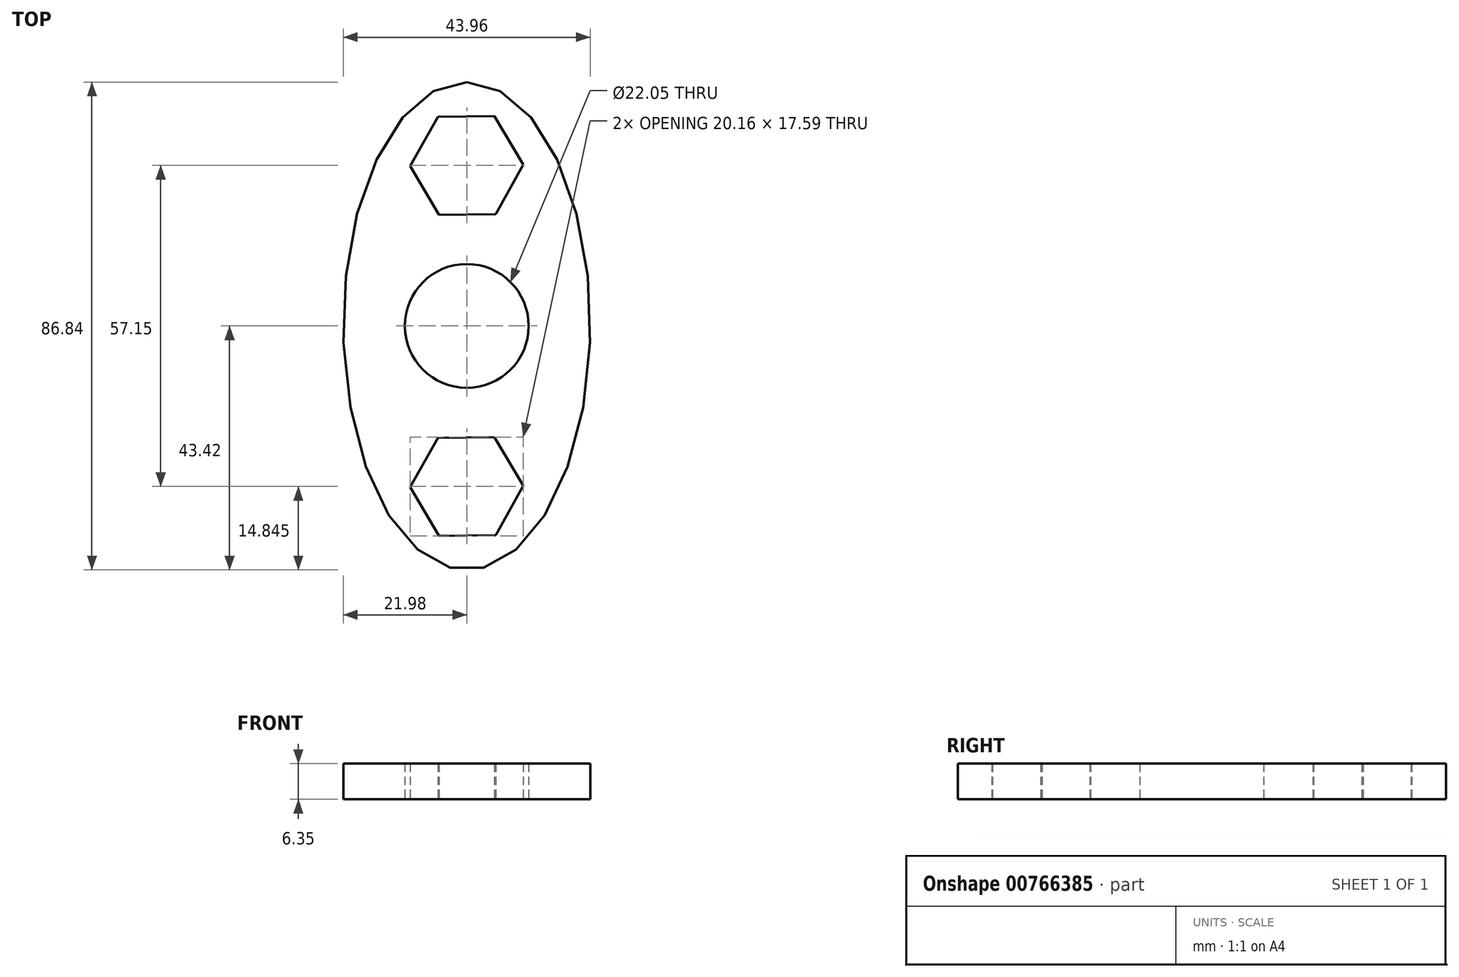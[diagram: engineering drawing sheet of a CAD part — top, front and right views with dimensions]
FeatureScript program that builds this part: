
annotation { "Feature Type Name" : "Feature", "Feature Type Description" : "" }
export const myFeature = defineFeature(function(context is Context, id is Id, definition is map)
    precondition{}
    {
        {
            var Q0;
            Q0=qCreatedBy(makeId("Top.planeOp"),FACE);
            var sketch = newSketch(context, id + "F0", { "sketchPlane" : qUnion([Q0])});
            skCircle(sketch, "E0", {"center": v(0, 0) * mm, "radius": 11.02 * mm});
            skCircle(sketch, "E1", {"center": v(0, 0) * mm, "radius": 14.29 * mm});
            skCircle(sketch, "E2.cCircle", {"center": v(0, 28.58) * mm, "radius": 8.73 * mm, "construction": true});
            skLineSegment(sketch, "E2.0", {"start": v(10.08, 28.7) * mm, "end": v(5.16, 19.91) * mm});
            skLineSegment(sketch, "E2.1", {"start": v(5.16, 19.91) * mm, "end": v(-4.93, 19.78) * mm});
            skLineSegment(sketch, "E2.2", {"start": v(-4.93, 19.78) * mm, "end": v(-10.08, 28.44) * mm});
            skLineSegment(sketch, "E2.3", {"start": v(-10.08, 28.44) * mm, "end": v(-5.16, 37.24) * mm});
            skLineSegment(sketch, "E2.4", {"start": v(-5.16, 37.24) * mm, "end": v(4.93, 37.37) * mm});
            skLineSegment(sketch, "E2.5", {"start": v(4.93, 37.37) * mm, "end": v(10.08, 28.7) * mm});
            skPoint(sketch, "E2.0.midPoint", {"position": v(7.62, 24.3) * mm});
            skCircle(sketch, "E3.cCircle", {"center": v(0, 28.58) * mm, "radius": 11.11 * mm, "construction": true});
            skLineSegment(sketch, "E3.0", {"start": v(6.21, 39.8) * mm, "end": v(12.83, 28.81) * mm});
            skLineSegment(sketch, "E3.1", {"start": v(12.83, 28.81) * mm, "end": v(6.62, 17.58) * mm});
            skLineSegment(sketch, "E3.2", {"start": v(6.62, 17.58) * mm, "end": v(-6.21, 17.35) * mm});
            skLineSegment(sketch, "E3.3", {"start": v(-6.21, 17.35) * mm, "end": v(-12.83, 28.34) * mm});
            skLineSegment(sketch, "E3.4", {"start": v(-12.83, 28.34) * mm, "end": v(-6.62, 39.57) * mm});
            skLineSegment(sketch, "E3.5", {"start": v(-6.62, 39.57) * mm, "end": v(6.21, 39.8) * mm});
            skPoint(sketch, "E3.0.midPoint", {"position": v(9.52, 34.3) * mm});
            skPoint(sketch, "E4.1.0", {"position": v(-9.52, -34.3) * mm});
            skCircle(sketch, "E4.1.1", {"center": v(0, -28.58) * mm, "radius": 8.73 * mm, "construction": true});
            skLineSegment(sketch, "E4.1.2", {"start": v(12.83, -28.34) * mm, "end": v(6.62, -39.57) * mm});
            skLineSegment(sketch, "E4.1.3", {"start": v(6.62, -39.57) * mm, "end": v(-6.21, -39.8) * mm});
            skCircle(sketch, "E4.1.4", {"center": v(0, -28.58) * mm, "radius": 11.11 * mm, "construction": true});
            skPoint(sketch, "E4.1.5", {"position": v(-7.62, -24.3) * mm});
            skLineSegment(sketch, "E4.1.6", {"start": v(5.16, -37.24) * mm, "end": v(-4.93, -37.37) * mm});
            skLineSegment(sketch, "E4.1.7", {"start": v(-6.21, -39.8) * mm, "end": v(-12.83, -28.81) * mm});
            skLineSegment(sketch, "E4.1.8", {"start": v(6.21, -17.35) * mm, "end": v(12.83, -28.34) * mm});
            skLineSegment(sketch, "E4.1.9", {"start": v(4.93, -19.78) * mm, "end": v(10.08, -28.44) * mm});
            skLineSegment(sketch, "E4.1.10", {"start": v(-5.16, -19.91) * mm, "end": v(4.93, -19.78) * mm});
            skLineSegment(sketch, "E4.1.11", {"start": v(-10.08, -28.7) * mm, "end": v(-5.16, -19.91) * mm});
            skLineSegment(sketch, "E4.1.12", {"start": v(-12.83, -28.81) * mm, "end": v(-6.62, -17.58) * mm});
            skLineSegment(sketch, "E4.1.13", {"start": v(-6.62, -17.58) * mm, "end": v(6.21, -17.35) * mm});
            skLineSegment(sketch, "E4.1.14", {"start": v(-4.93, -37.37) * mm, "end": v(-10.08, -28.7) * mm});
            skLineSegment(sketch, "E4.1.15", {"start": v(10.08, -28.44) * mm, "end": v(5.16, -37.24) * mm});
            skEllipse(sketch, "E5", {"center": v(0, 0) * mm, "majorRadius": 43.42 * mm, "minorRadius": 21.98 * mm, "majorAxis": v(0, 1)});
            skSolve(sketch);
        }
        {
            var Q0;
            Q0=makeQuery(id+"F0.imprint","IMPRINT",FACE,{"disambiguationData":[TD([[makeQuery(id+"F0.imprint","IMPRINT",EDGE,{"derivedFrom":sQuery(id+"F0.wireOp",EDGE,"E1")}),-1.0]])]});
            var Q1;
            Q1=makeQuery(id+"F0.imprint","IMPRINT",FACE,{"disambiguationData":[TD([[makeQuery(id+"F0.imprint","IMPRINT",EDGE,{"derivedFrom":sQuery(id+"F0.wireOp",EDGE,"E2.0")}),1.0]])]});
            var Q2;
            Q2=makeQuery(id+"F0.imprint","IMPRINT",FACE,{"disambiguationData":[TD([[makeQuery(id+"F0.imprint","IMPRINT",EDGE,{"derivedFrom":sQuery(id+"F0.wireOp",EDGE,"E0")}),-1.0]])]});
            var Q3;
            Q3=makeQuery(id+"F0.imprint","IMPRINT",FACE,{"disambiguationData":[TD([[makeQuery(id+"F0.imprint","IMPRINT",EDGE,{"derivedFrom":sQuery(id+"F0.wireOp",EDGE,"E4.1.2")}),-1.0]])]});
            extrude(context, id + "F1", {"entities" : qUnion([Q0, Q1, Q2, Q3]), "depth" : 6.35 * mm, "offsetDistance" : 25.4 * mm});
        }
    });
